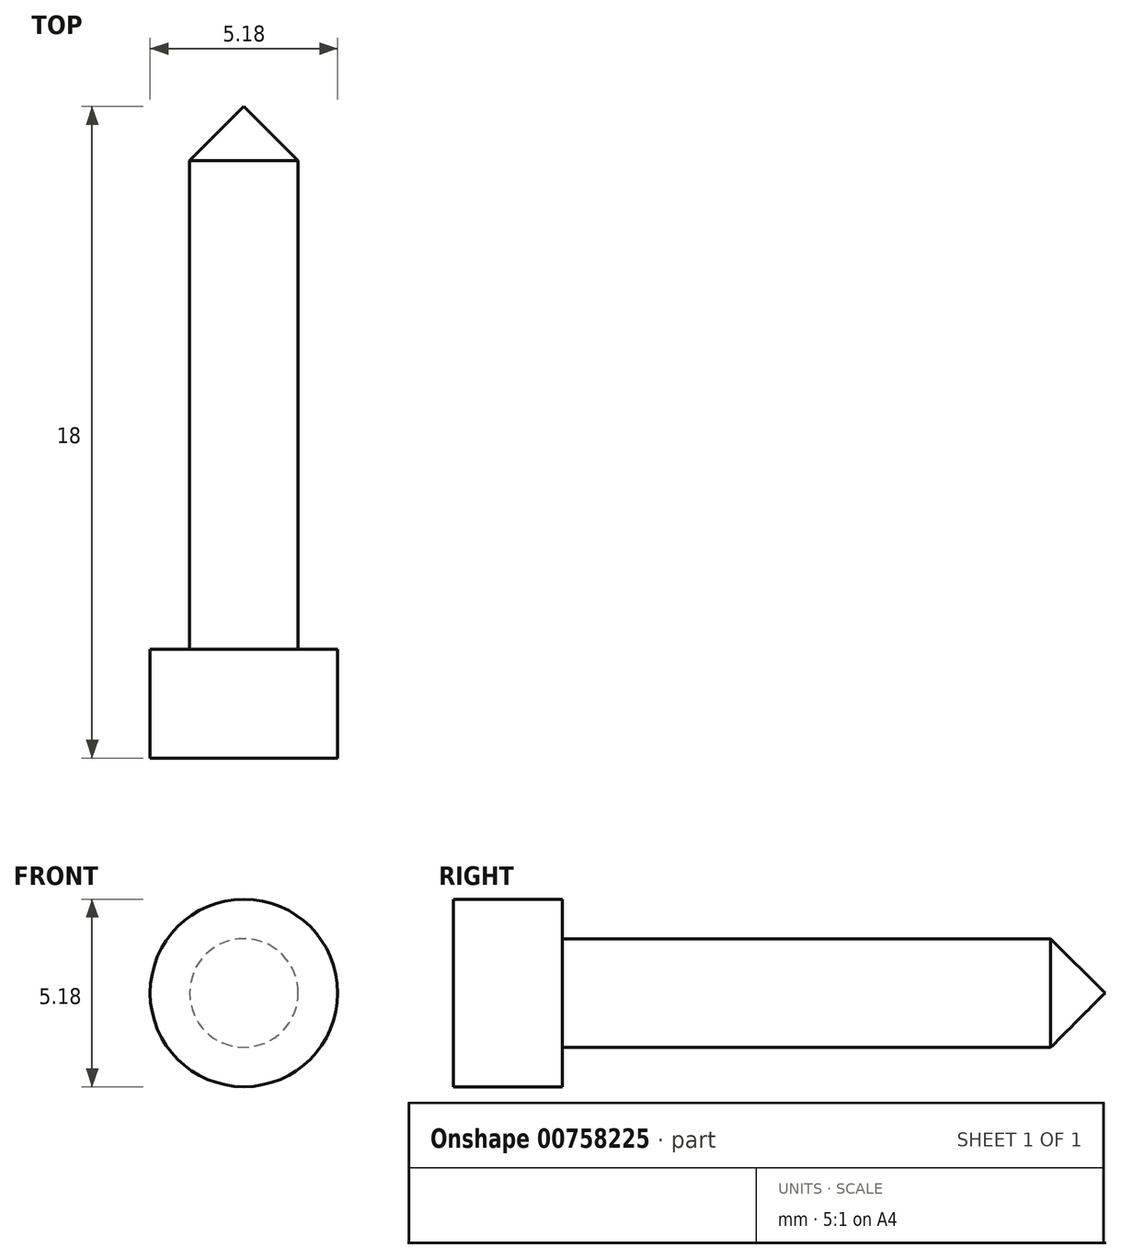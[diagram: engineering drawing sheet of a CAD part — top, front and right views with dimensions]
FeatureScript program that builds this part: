
annotation { "Feature Type Name" : "Feature", "Feature Type Description" : "" }
export const myFeature = defineFeature(function(context is Context, id is Id, definition is map)
    precondition{}
    {
        {
            var Q0;
            Q0=qCreatedBy(makeId("Front.planeOp"),FACE);
            var sketch = newSketch(context, id + "F0", { "sketchPlane" : qUnion([Q0])});
            skCircle(sketch, "E0", {"center": v(0, 0) * mm, "radius": 1.5 * mm});
            skSolve(sketch);
        }
        {
            var Q0;
            Q0 = qSketchRegion(id + "F0", true);
            extrude(context, id + "F1", {"entities" : qUnion([Q0]), "depth" : 15 * mm, "offsetDistance" : 25 * mm});
        }
        {
            var Q0;
            Q0=makeQuery(id+"F1.opExtrude","CAP_FACE",FACE,{"disambiguationData":[OSD([sQuery(id+"F0.wireOp",EDGE,"E0")])],"isStart":false});
            var sketch = newSketch(context, id + "F2", { "sketchPlane" : qUnion([Q0])});
            skCircle(sketch, "E1", {"center": v(0, 0) * mm, "radius": 2.6 * mm});
            skSolve(sketch);
        }
        {
            var Q0;
            Q0 = qSketchRegion(id + "F2", true);
            extrude(context, id + "F3", {"entities" : qUnion([Q0]), "operationType" : NewBodyOperationType.ADD, "depth" : 3 * mm, "offsetDistance" : 25 * mm});
        }
        {
            var Q0;
            Q0=makeQuery(id+"F1.opExtrude","CAP_EDGE",EDGE,{"disambiguationData":[OSD([sQuery(id+"F0.wireOp",EDGE,"E0")])],"isStart":true});
            chamfer(context, id + "F4", {"entities" : qUnion([Q0]), "width" : 1.5 * mm, "tangentPropagation" : true});
        }
    });
